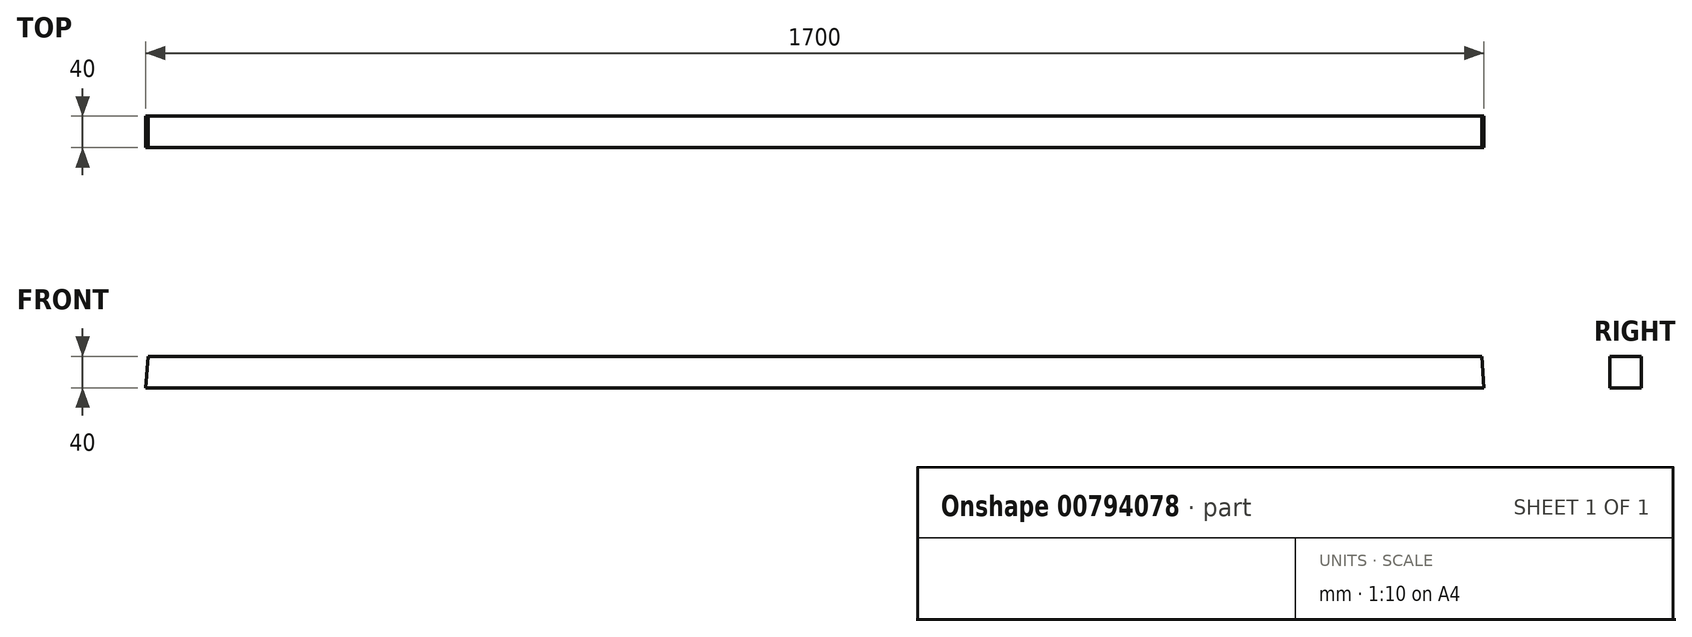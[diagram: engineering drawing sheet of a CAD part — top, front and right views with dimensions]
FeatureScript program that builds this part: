
annotation { "Feature Type Name" : "Feature", "Feature Type Description" : "" }
export const myFeature = defineFeature(function(context is Context, id is Id, definition is map)
    precondition{}
    {
        {
            var Q0;
            Q0=qCreatedBy(makeId("Front.planeOp"),FACE);
            var sketch = newSketch(context, id + "F0", { "sketchPlane" : qUnion([Q0])});
            skLineSegment(sketch, "E0.bottom", {"start": v(0, 0) * mm, "end": v(-1700, 0) * mm});
            skLineSegment(sketch, "E0.top", {"start": v(-2.8, 40) * mm, "end": v(-1697.2, 40) * mm});
            skLineSegment(sketch, "E1", {"start": v(0, 0) * mm, "end": v(-3.42, 48.92) * mm});
            skLineSegment(sketch, "E2", {"start": v(-850, 0) * mm, "end": v(-850, 69.52) * mm, "construction": true});
            skLineSegment(sketch, "E3.MirrorCS", {"start": v(-1700, 0) * mm, "end": v(-1696.58, 48.92) * mm});
            skSolve(sketch);
        }
        {
            var Q0;
            Q0 = qSketchRegion(id + "F0", true);
            extrude(context, id + "F1", {"entities" : qUnion([Q0]), "depth" : 40 * mm, "offsetDistance" : 25 * mm});
        }
    });
